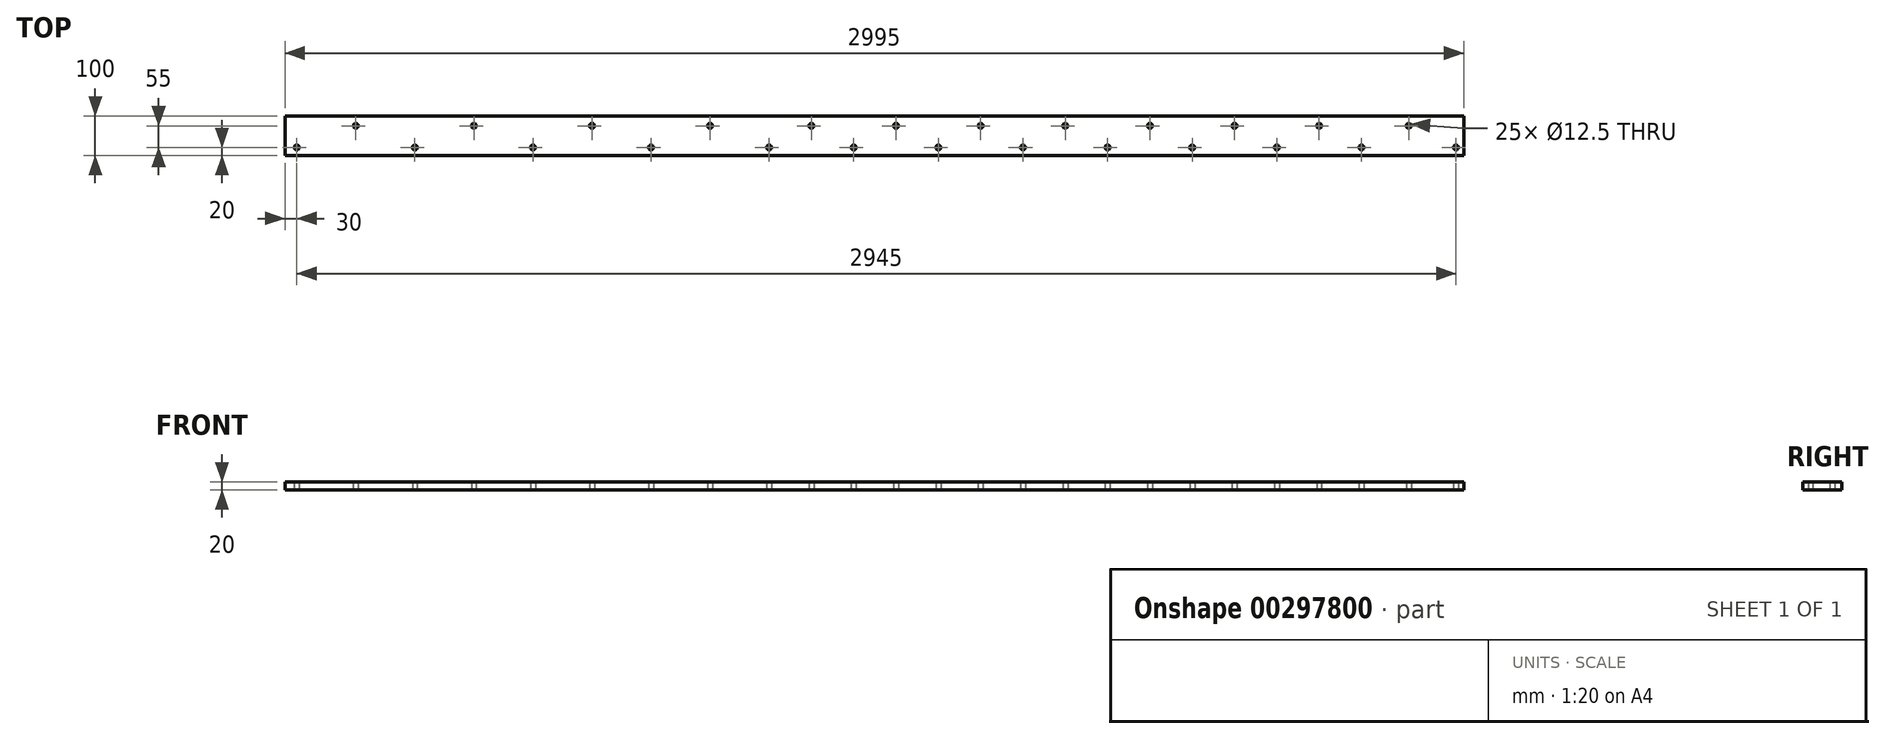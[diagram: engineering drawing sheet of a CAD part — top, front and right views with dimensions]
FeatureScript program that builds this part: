
annotation { "Feature Type Name" : "Feature", "Feature Type Description" : "" }
export const myFeature = defineFeature(function(context is Context, id is Id, definition is map)
    precondition{}
    {
        {
            var Q0;
            Q0=qCreatedBy(makeId("Top.planeOp"),FACE);
            var sketch = newSketch(context, id + "F0", { "sketchPlane" : qUnion([Q0])});
            skLineSegment(sketch, "E0.bottom", {"start": v(0, 0) * mm, "end": v(2995, 0) * mm});
            skLineSegment(sketch, "E0.top", {"start": v(0, -100) * mm, "end": v(2995, -100) * mm});
            skLineSegment(sketch, "E0.left", {"start": v(0, 0) * mm, "end": v(0, -100) * mm});
            skLineSegment(sketch, "E0.right", {"start": v(2995, 0) * mm, "end": v(2995, -100) * mm});
            skLineSegment(sketch, "E1", {"start": v(0, -25) * mm, "end": v(2995, -25) * mm, "construction": true});
            skLineSegment(sketch, "E2", {"start": v(0, -80) * mm, "end": v(2995, -80) * mm, "construction": true});
            skCircle(sketch, "E3", {"center": v(180, -25) * mm, "radius": 6.25 * mm});
            skCircle(sketch, "E4.1.0.0", {"center": v(480, -25) * mm, "radius": 6.25 * mm});
            skCircle(sketch, "E4.2.0.0", {"center": v(780, -25) * mm, "radius": 6.25 * mm});
            skCircle(sketch, "E4.3.0.0", {"center": v(1080, -25) * mm, "radius": 6.25 * mm});
            skLineSegment(sketch, "E4.direction1", {"start": v(180, -25) * mm, "end": v(480, -25) * mm, "construction": true});
            skCircle(sketch, "E5", {"center": v(30, -80) * mm, "radius": 6.25 * mm});
            skCircle(sketch, "E6.1.0.0", {"center": v(330, -80) * mm, "radius": 6.25 * mm});
            skCircle(sketch, "E6.2.0.0", {"center": v(630, -80) * mm, "radius": 6.25 * mm});
            skCircle(sketch, "E6.3.0.0", {"center": v(930, -80) * mm, "radius": 6.25 * mm});
            skCircle(sketch, "E6.4.0.0", {"center": v(1230, -80) * mm, "radius": 6.25 * mm});
            skLineSegment(sketch, "E6.direction1", {"start": v(30, -80) * mm, "end": v(330, -80) * mm, "construction": true});
            skCircle(sketch, "E7.1.0.0", {"center": v(1337.5, -25) * mm, "radius": 6.25 * mm});
            skLineSegment(sketch, "E7.direction1", {"start": v(1080, -25) * mm, "end": v(1337.5, -25) * mm, "construction": true});
            skCircle(sketch, "E8.1.0.0", {"center": v(1552.5, -25) * mm, "radius": 6.25 * mm});
            skCircle(sketch, "E8.2.0.0", {"center": v(1767.5, -25) * mm, "radius": 6.25 * mm});
            skCircle(sketch, "E8.3.0.0", {"center": v(1982.5, -25) * mm, "radius": 6.25 * mm});
            skCircle(sketch, "E8.4.0.0", {"center": v(2197.5, -25) * mm, "radius": 6.25 * mm});
            skCircle(sketch, "E8.5.0.0", {"center": v(2412.5, -25) * mm, "radius": 6.25 * mm});
            skCircle(sketch, "E8.6.0.0", {"center": v(2627.5, -25) * mm, "radius": 6.25 * mm});
            skLineSegment(sketch, "E8.direction1", {"start": v(1337.5, -25) * mm, "end": v(1552.5, -25) * mm, "construction": true});
            skCircle(sketch, "E9.1.0.0", {"center": v(1445, -80) * mm, "radius": 6.25 * mm});
            skCircle(sketch, "E9.2.0.0", {"center": v(1660, -80) * mm, "radius": 6.25 * mm});
            skCircle(sketch, "E9.3.0.0", {"center": v(1875, -80) * mm, "radius": 6.25 * mm});
            skCircle(sketch, "E9.4.0.0", {"center": v(2090, -80) * mm, "radius": 6.25 * mm});
            skCircle(sketch, "E9.5.0.0", {"center": v(2305, -80) * mm, "radius": 6.25 * mm});
            skCircle(sketch, "E9.6.0.0", {"center": v(2520, -80) * mm, "radius": 6.25 * mm});
            skCircle(sketch, "E9.7.0.0", {"center": v(2735, -80) * mm, "radius": 6.25 * mm});
            skLineSegment(sketch, "E9.direction1", {"start": v(1230, -80) * mm, "end": v(1445, -80) * mm, "construction": true});
            skCircle(sketch, "E10.1.0.0", {"center": v(2855, -25) * mm, "radius": 6.25 * mm});
            skLineSegment(sketch, "E10.direction1", {"start": v(2627.5, -25) * mm, "end": v(2855, -25) * mm, "construction": true});
            skCircle(sketch, "E11.1.0.0", {"center": v(2975, -80) * mm, "radius": 6.25 * mm});
            skLineSegment(sketch, "E11.direction1", {"start": v(2735, -80) * mm, "end": v(2975, -80) * mm, "construction": true});
            skSolve(sketch);
        }
        {
            var Q0;
            Q0 = qSketchRegion(id + "F0", true);
            extrude(context, id + "F1", {"entities" : qUnion([Q0]), "depth" : 20 * mm});
        }
    });
